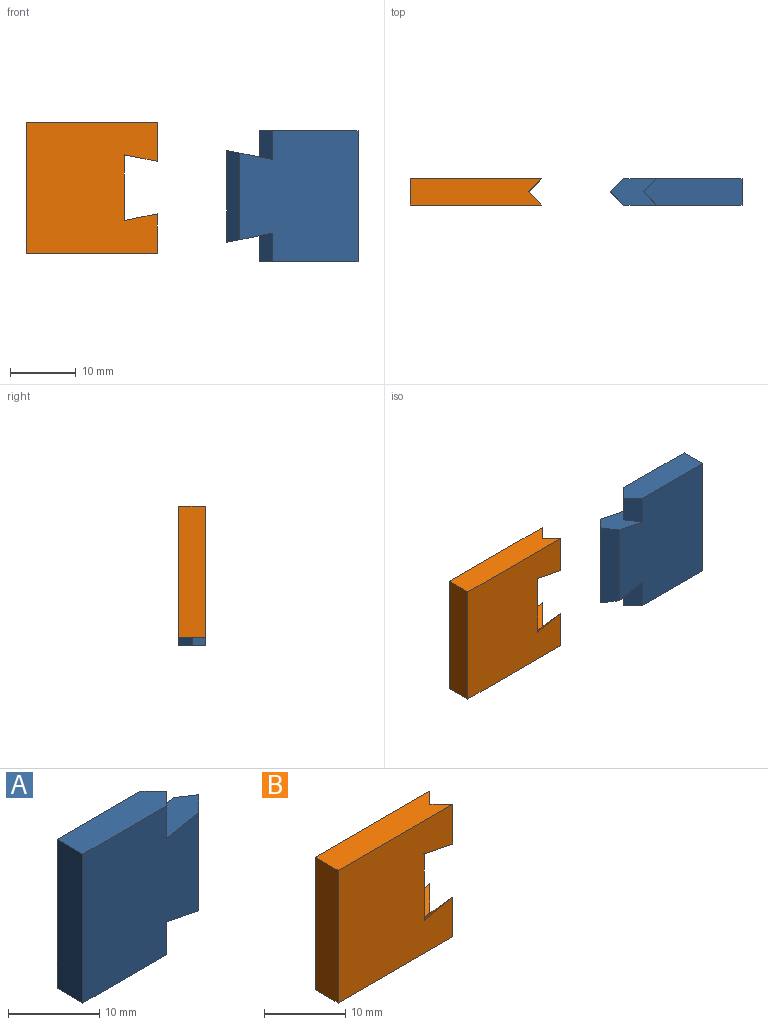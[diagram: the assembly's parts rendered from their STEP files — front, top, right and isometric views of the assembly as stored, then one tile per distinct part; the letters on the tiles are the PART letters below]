
ASSEMBLY  parts=2 mates=1
PART A: 13 faces, bbox 20x4x20 mm
  f0: plane 15x4mm, normal (0,0,1), area 56mm2, adj f1,f5,f6,f11,f12
  f1: plane 20x4mm, normal (-1,0,0), area 80mm2, adj f0,f2,f5,f6
  f2: plane 15x4mm, normal (0,0,-1), area 56mm2, adj f1,f5,f6,f7,f8
  f3: plane 7x4mm, normal (-0.2,0,-0.98), area 20.4mm2, adj f5,f6,f7,f8,f9,f10
  f4: plane 7x4mm, normal (-0.2,0,0.98), area 20.4mm2, adj f5,f6,f9,f10,f11,f12
  f5: plane 20x18mm, normal (0,-1,0), area 321mm2, adj f0,f1,f2,f3,f4,f8,f9,f12
  f6: plane 20x18mm, normal (0,1,0), area 321mm2, adj f0,f1,f2,f3,f4,f7,f10,f11
  f7: plane 4.4x2mm, normal (0.71,0.71,0), area 11.9mm2, adj f2,f3,f6,f8
  f8: plane 4.4x2mm, normal (0.71,-0.71,0), area 11.9mm2, adj f2,f3,f5,f7
  f9: plane 14x2mm, normal (0.71,-0.71,0), area 38.5mm2, adj f3,f4,f5,f10
  f10: plane 14x2mm, normal (0.71,0.71,0), area 38.5mm2, adj f3,f4,f6,f9
  f11: plane 4.4x2mm, normal (0.71,0.71,0), area 11.9mm2, adj f0,f4,f6,f12
  f12: plane 4.4x2mm, normal (0.71,-0.71,0), area 11.9mm2, adj f0,f4,f5,f11
PART B: 15 faces, bbox 20x4x20 mm
  f0: plane 20x4mm, normal (0,0,1), area 76mm2, adj f1,f3,f4,f9,f10
  f1: plane 20x4mm, normal (-1,0,0), area 80mm2, adj f0,f2,f3,f9
  f2: plane 20x4mm, normal (0,0,-1), area 76mm2, adj f1,f3,f7,f9,f13
  f3: plane 20x20mm, normal (0,-1,0), area 355mm2, adj f0,f1,f2,f4,f5,f6,f7,f8
  f4: plane 6x2mm, normal (0.71,0.71,0), area 13.5mm2, adj f0,f3,f5,f10
  f5: plane 7x3.44mm, normal (-0.14,0.71,-0.69), area 14.4mm2, adj f3,f4,f6,f11
  f6: plane 14.88x2mm, normal (0.71,0.71,0), area 35.2mm2, adj f3,f5,f8,f12
  f7: plane 6x2mm, normal (0.71,0.71,0), area 13.5mm2, adj f2,f3,f8,f13
  f8: plane 7x3.44mm, normal (-0.14,0.71,0.69), area 14.4mm2, adj f3,f6,f7,f14
  f9: plane 20x20mm, normal (0,1,0), area 355mm2, adj f0,f1,f2,f10,f11,f12,f13,f14
  f10: plane 6x2mm, normal (0.71,-0.71,0), area 13.5mm2, adj f0,f4,f9,f11
  f11: plane 7x3.44mm, normal (-0.14,-0.71,-0.69), area 14.4mm2, adj f5,f9,f10,f12
  f12: plane 14.88x2mm, normal (0.71,-0.71,0), area 35.2mm2, adj f6,f9,f11,f14
  f13: plane 6x2mm, normal (0.71,-0.71,0), area 13.5mm2, adj f2,f7,f9,f14
  f14: plane 7x3.44mm, normal (-0.14,-0.71,0.69), area 14.4mm2, adj f8,f9,f12,f13
PLACE A rot(axis=(0,1,0),180deg) t=(16.95,-2.74,-13.45)mm
PLACE B t=(-33.63,-4.74,7.88)mm
MATE planar A.f5 <-> B.f3  axis (0,-1,0) through (-1.05,-6.74,-3.45)mm
